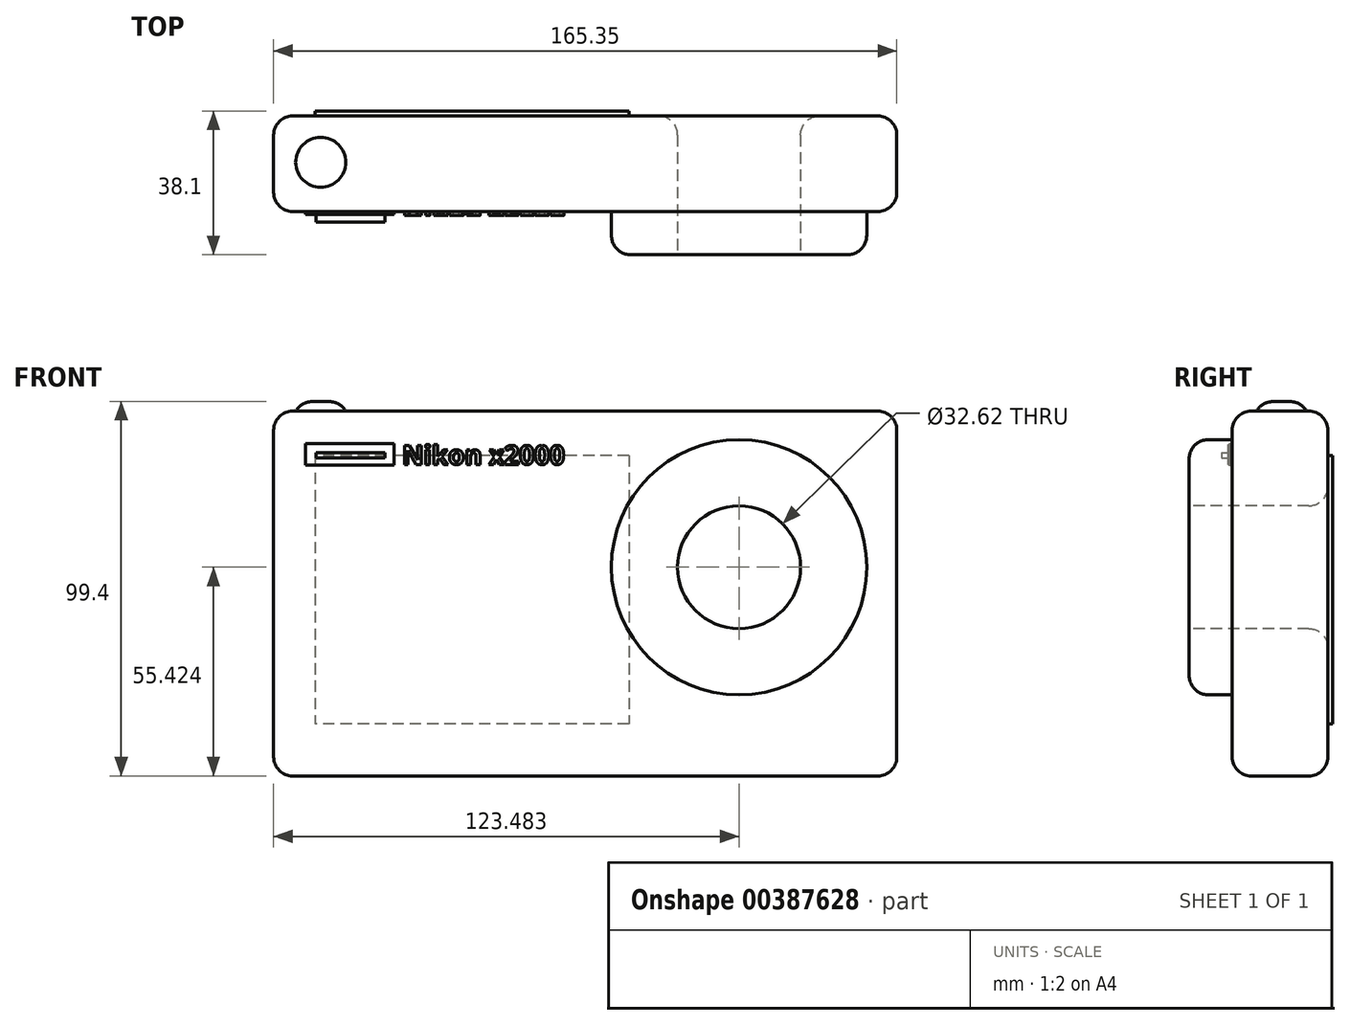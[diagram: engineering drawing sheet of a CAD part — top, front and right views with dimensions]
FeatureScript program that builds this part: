
annotation { "Feature Type Name" : "Feature", "Feature Type Description" : "" }
export const myFeature = defineFeature(function(context is Context, id is Id, definition is map)
    precondition{}
    {
        {
            var Q0;
            Q0=qCreatedBy(makeId("Front.planeOp"),FACE);
            var sketch = newSketch(context, id + "F0", { "sketchPlane" : qUnion([Q0])});
            skLineSegment(sketch, "E0.bottom", {"start": v(-79.95, 75.5) * mm, "end": v(85.4, 75.5) * mm});
            skLineSegment(sketch, "E0.top", {"start": v(-79.95, -21.35) * mm, "end": v(85.4, -21.35) * mm});
            skLineSegment(sketch, "E0.left", {"start": v(-79.95, 75.5) * mm, "end": v(-79.95, -21.35) * mm});
            skLineSegment(sketch, "E0.right", {"start": v(85.4, 75.5) * mm, "end": v(85.4, -21.35) * mm});
            skSolve(sketch);
        }
        {
            var Q0;
            Q0=makeQuery(id+"F0.imprint","IMPRINT",FACE,{"disambiguationData":[TD([[makeQuery(id+"F0.imprint","IMPRINT",EDGE,{"derivedFrom":sQuery(id+"F0.wireOp",EDGE,"E0.bottom")}),-1.0]])]});
            extrude(context, id + "F1", {"entities" : qUnion([Q0]), "depth" : 25.4 * mm});
        }
        {
            var Q0;
            Q0=makeQuery(id+"F1.opExtrude","CAP_FACE",FACE,{"disambiguationData":[OSD([sQuery(id+"F0.wireOp",EDGE,"E0.bottom"),sQuery(id+"F0.wireOp",EDGE,"E0.top"),sQuery(id+"F0.wireOp",EDGE,"E0.left"),sQuery(id+"F0.wireOp",EDGE,"E0.right")])],"isStart":false});
            var sketch = newSketch(context, id + "F2", { "sketchPlane" : qUnion([Q0])});
            skCircle(sketch, "E1", {"center": v(43.53, 34.07) * mm, "radius": 33.87 * mm});
            skSolve(sketch);
        }
        {
            var Q0;
            Q0=makeQuery(id+"F2.imprint","IMPRINT",FACE,{"disambiguationData":[TD([[makeQuery(id+"F2.imprint","IMPRINT",EDGE,{"derivedFrom":sQuery(id+"F2.wireOp",EDGE,"E1")}),1.0]])]});
            extrude(context, id + "F3", {"entities" : qUnion([Q0]), "operationType" : NewBodyOperationType.ADD, "depth" : 11.43 * mm});
        }
        {
            var Q0;
            Q0=makeQuery(id+"F3.opExtrude","CAP_FACE",FACE,{"disambiguationData":[OSD([sQuery(id+"F2.wireOp",EDGE,"E1")])],"isStart":false});
            var sketch = newSketch(context, id + "F4", { "sketchPlane" : qUnion([Q0])});
            skCircle(sketch, "E2", {"center": v(43.53, 34.07) * mm, "radius": 16.31 * mm});
            skSolve(sketch);
        }
        {
            var Q0;
            Q0=makeQuery(id+"F4.imprint","IMPRINT",FACE,{"disambiguationData":[TD([[makeQuery(id+"F4.imprint","IMPRINT",EDGE,{"derivedFrom":sQuery(id+"F4.wireOp",EDGE,"E2")}),1.0]])]});
            extrude(context, id + "F5", {"entities" : qUnion([Q0]), "operationType" : NewBodyOperationType.REMOVE, "endBound" : BoundingType.THROUGH_ALL, "oppositeDirection" : true, "depth" : 25.4 * mm});
        }
        {
            var Q0;
            Q0=makeQuery(id+"F3.opExtrude","CAP_EDGE",EDGE,{"disambiguationData":[OSD([sQuery(id+"F2.wireOp",EDGE,"E1")])],"isStart":false});
            var Q1;
            Q1=makeQuery(id+"F5.boolean.opBoolean","COPY",EDGE,{"derivedFrom":makeQuery(id+"F5.opExtrude","CAP_EDGE",EDGE,{"disambiguationData":[OSD([sQuery(id+"F4.wireOp",EDGE,"E2")])],"isStart":true})});
            var Q2;
            Q2=makeQuery(id+"F1.opExtrude","CAP_EDGE",EDGE,{"disambiguationData":[OSD([sQuery(id+"F0.wireOp",EDGE,"E0.bottom")])],"isStart":false});
            var Q3;
            Q3=makeQuery(id+"F1.opExtrude","CAP_EDGE",EDGE,{"disambiguationData":[OSD([sQuery(id+"F0.wireOp",EDGE,"E0.right")])],"isStart":false});
            var Q4;
            Q4=makeQuery(id+"F1.opExtrude","CAP_EDGE",EDGE,{"disambiguationData":[OSD([sQuery(id+"F0.wireOp",EDGE,"E0.left")])],"isStart":false});
            var Q5;
            Q5=makeQuery(id+"F1.opExtrude","CAP_EDGE",EDGE,{"disambiguationData":[OSD([sQuery(id+"F0.wireOp",EDGE,"E0.top")])],"isStart":false});
            fillet(context, id + "F6", {"entities" : qUnion([Q0, Q1, Q2, Q3, Q4, Q5]), "radius" : 5.08 * mm, "tangentPropagation" : true, "allowEdgeOverflow" : false});
        }
        {
            var Q0;
            Q0=makeQuery(id+"F5.boolean.opBoolean","INTERSECT",EDGE,{"derivedFrom":[makeQuery(id+"F1.opExtrude","CAP_FACE",FACE,{"disambiguationData":[OSD([sQuery(id+"F0.wireOp",EDGE,"E0.bottom"),sQuery(id+"F0.wireOp",EDGE,"E0.top"),sQuery(id+"F0.wireOp",EDGE,"E0.left"),sQuery(id+"F0.wireOp",EDGE,"E0.right")])],"isStart":true}),makeQuery(id+"F5.opExtrude","SWEPT_FACE",FACE,{"disambiguationData":[OSD([sQuery(id+"F4.wireOp",EDGE,"E2")])]})]});
            var Q1;
            Q1=makeQuery(id+"F1.opExtrude","CAP_EDGE",EDGE,{"disambiguationData":[OSD([sQuery(id+"F0.wireOp",EDGE,"E0.right")])],"isStart":true});
            var Q2;
            Q2=makeQuery(id+"F1.opExtrude","CAP_EDGE",EDGE,{"disambiguationData":[OSD([sQuery(id+"F0.wireOp",EDGE,"E0.bottom")])],"isStart":true});
            var Q3;
            Q3=makeQuery(id+"F1.opExtrude","CAP_EDGE",EDGE,{"disambiguationData":[OSD([sQuery(id+"F0.wireOp",EDGE,"E0.top")])],"isStart":true});
            var Q4;
            Q4=makeQuery(id+"F1.opExtrude","CAP_EDGE",EDGE,{"disambiguationData":[OSD([sQuery(id+"F0.wireOp",EDGE,"E0.left")])],"isStart":true});
            fillet(context, id + "F7", {"entities" : qUnion([Q0, Q1, Q2, Q3, Q4]), "radius" : 5.08 * mm, "tangentPropagation" : true, "allowEdgeOverflow" : false});
        }
        {
            var Q0;
            Q0=makeQuery(id+"F1.opExtrude","SWEPT_EDGE",EDGE,{"disambiguationData":[OSD([sQuery(id+"F0.wireOp",EDGE,"E0.bottom"),sQuery(id+"F0.wireOp",EDGE,"E0.right")])]});
            var Q1;
            Q1=makeQuery(id+"F1.opExtrude","SWEPT_EDGE",EDGE,{"disambiguationData":[OSD([sQuery(id+"F0.wireOp",EDGE,"E0.top"),sQuery(id+"F0.wireOp",EDGE,"E0.right")])]});
            var Q2;
            Q2=makeQuery(id+"F1.opExtrude","SWEPT_EDGE",EDGE,{"disambiguationData":[OSD([sQuery(id+"F0.wireOp",EDGE,"E0.top"),sQuery(id+"F0.wireOp",EDGE,"E0.left")])]});
            var Q3;
            Q3=makeQuery(id+"F1.opExtrude","SWEPT_EDGE",EDGE,{"disambiguationData":[OSD([sQuery(id+"F0.wireOp",EDGE,"E0.bottom"),sQuery(id+"F0.wireOp",EDGE,"E0.left")])]});
            fillet(context, id + "F8", {"entities" : qUnion([Q0, Q1, Q2, Q3]), "radius" : 5.08 * mm, "tangentPropagation" : true, "allowEdgeOverflow" : false});
        }
        {
            var Q0;
            Q0=makeQuery(id+"F1.opExtrude","SWEPT_FACE",FACE,{"disambiguationData":[OSD([sQuery(id+"F0.wireOp",EDGE,"E0.bottom")])]});
            var sketch = newSketch(context, id + "F9", { "sketchPlane" : qUnion([Q0])});
            skCircle(sketch, "E3", {"center": v(-67.46, -12.31) * mm, "radius": 6.65 * mm});
            skSolve(sketch);
        }
        {
            var Q0;
            Q0=makeQuery(id+"F9.imprint","IMPRINT",FACE,{"disambiguationData":[TD([[makeQuery(id+"F9.imprint","IMPRINT",EDGE,{"derivedFrom":sQuery(id+"F9.wireOp",EDGE,"E3")}),1.0]])]});
            extrude(context, id + "F10", {"entities" : qUnion([Q0]), "operationType" : NewBodyOperationType.ADD, "depth" : 2.54 * mm});
        }
        {
            var Q0;
            Q0=makeQuery(id+"F10.opExtrude","CAP_EDGE",EDGE,{"disambiguationData":[OSD([sQuery(id+"F9.wireOp",EDGE,"E3")])],"isStart":false});
            fillet(context, id + "F11", {"entities" : qUnion([Q0]), "radius" : 5.08 * mm, "tangentPropagation" : true, "allowEdgeOverflow" : false});
        }
        {
            var Q0;
            Q0=makeQuery(id+"F1.opExtrude","CAP_FACE",FACE,{"disambiguationData":[OSD([sQuery(id+"F0.wireOp",EDGE,"E0.bottom"),sQuery(id+"F0.wireOp",EDGE,"E0.top"),sQuery(id+"F0.wireOp",EDGE,"E0.left"),sQuery(id+"F0.wireOp",EDGE,"E0.right")])],"isStart":true});
            var sketch = newSketch(context, id + "F12", { "sketchPlane" : qUnion([Q0])});
            skLineSegment(sketch, "E4.bottom", {"start": v(-14.35, 63.77) * mm, "end": v(68.95, 63.77) * mm});
            skLineSegment(sketch, "E4.top", {"start": v(-14.35, -7.5) * mm, "end": v(68.95, -7.5) * mm});
            skLineSegment(sketch, "E4.left", {"start": v(-14.35, 63.77) * mm, "end": v(-14.35, -7.5) * mm});
            skLineSegment(sketch, "E4.right", {"start": v(68.95, 63.77) * mm, "end": v(68.95, -7.5) * mm});
            skSolve(sketch);
        }
        {
            var Q0;
            Q0=makeQuery(id+"F12.imprint","IMPRINT",FACE,{"disambiguationData":[TD([[makeQuery(id+"F12.imprint","IMPRINT",EDGE,{"derivedFrom":sQuery(id+"F12.wireOp",EDGE,"E4.bottom")}),-1.0]])]});
            extrude(context, id + "F13", {"entities" : qUnion([Q0]), "operationType" : NewBodyOperationType.ADD, "depth" : 1.27 * mm});
        }
        {
            var Q0;
            Q0=makeQuery(id+"F1.opExtrude","CAP_FACE",FACE,{"disambiguationData":[OSD([sQuery(id+"F0.wireOp",EDGE,"E0.bottom"),sQuery(id+"F0.wireOp",EDGE,"E0.top"),sQuery(id+"F0.wireOp",EDGE,"E0.left"),sQuery(id+"F0.wireOp",EDGE,"E0.right")])],"isStart":false});
            var sketch = newSketch(context, id + "F14", { "sketchPlane" : qUnion([Q0])});
            skLineSegment(sketch, "E5.bottom", {"start": v(-71.52, 66.89) * mm, "end": v(-48.02, 66.89) * mm});
            skLineSegment(sketch, "E5.top", {"start": v(-71.52, 61.2) * mm, "end": v(-48.02, 61.2) * mm});
            skLineSegment(sketch, "E5.left", {"start": v(-71.52, 66.89) * mm, "end": v(-71.52, 61.2) * mm});
            skLineSegment(sketch, "E5.right", {"start": v(-48.02, 66.89) * mm, "end": v(-48.02, 61.2) * mm});
            skSolve(sketch);
        }
        {
            var Q0;
            Q0=makeQuery(id+"F14.imprint","IMPRINT",FACE,{"disambiguationData":[TD([[makeQuery(id+"F14.imprint","IMPRINT",EDGE,{"derivedFrom":sQuery(id+"F14.wireOp",EDGE,"E5.bottom")}),-1.0]])]});
            extrude(context, id + "F15", {"entities" : qUnion([Q0]), "operationType" : NewBodyOperationType.ADD, "depth" : 0.76 * mm});
        }
        {
            var Q0;
            Q0=makeQuery(id+"F1.opExtrude","CAP_FACE",FACE,{"disambiguationData":[OSD([sQuery(id+"F0.wireOp",EDGE,"E0.bottom"),sQuery(id+"F0.wireOp",EDGE,"E0.top"),sQuery(id+"F0.wireOp",EDGE,"E0.left"),sQuery(id+"F0.wireOp",EDGE,"E0.right")])],"isStart":false});
            var sketch = newSketch(context, id + "F16", { "sketchPlane" : qUnion([Q0])});
            skText(sketch, "E6", { "text": "Nikon x2000\n", "fontName": "OpenSans-Bold.ttf"});
            const initialGuessF16  = {"E6": [-0.04586, 0.06135, 1, 0, 0.00506]};
            skSetInitialGuess(sketch, initialGuessF16);
            skSolve(sketch);
        }
        {
            var Q0;
            Q0 = qSketchRegion(id + "F16", true);
            extrude(context, id + "F17", {"entities" : qUnion([Q0]), "operationType" : NewBodyOperationType.ADD, "depth" : 1.02 * mm});
        }
        {
            var Q0;
            Q0=makeQuery(id+"F15.opExtrude","CAP_FACE",FACE,{"disambiguationData":[OSD([sQuery(id+"F14.wireOp",EDGE,"E5.bottom"),sQuery(id+"F14.wireOp",EDGE,"E5.top"),sQuery(id+"F14.wireOp",EDGE,"E5.left"),sQuery(id+"F14.wireOp",EDGE,"E5.right")])],"isStart":false});
            var sketch = newSketch(context, id + "F18", { "sketchPlane" : qUnion([Q0])});
            skLineSegment(sketch, "E7.bottom", {"start": v(-68.74, 64.53) * mm, "end": v(-50.43, 64.53) * mm});
            skLineSegment(sketch, "E7.top", {"start": v(-68.74, 63.08) * mm, "end": v(-50.43, 63.08) * mm});
            skLineSegment(sketch, "E7.left", {"start": v(-68.74, 64.53) * mm, "end": v(-68.74, 63.08) * mm});
            skLineSegment(sketch, "E7.right", {"start": v(-50.43, 64.53) * mm, "end": v(-50.43, 63.08) * mm});
            skSolve(sketch);
        }
        {
            var Q0;
            Q0=makeQuery(id+"F18.imprint","IMPRINT",FACE,{"disambiguationData":[TD([[makeQuery(id+"F18.imprint","IMPRINT",EDGE,{"derivedFrom":sQuery(id+"F18.wireOp",EDGE,"E7.bottom")}),-1.0]])]});
            extrude(context, id + "F19", {"entities" : qUnion([Q0]), "operationType" : NewBodyOperationType.ADD, "depth" : 2.03 * mm});
        }
    });
